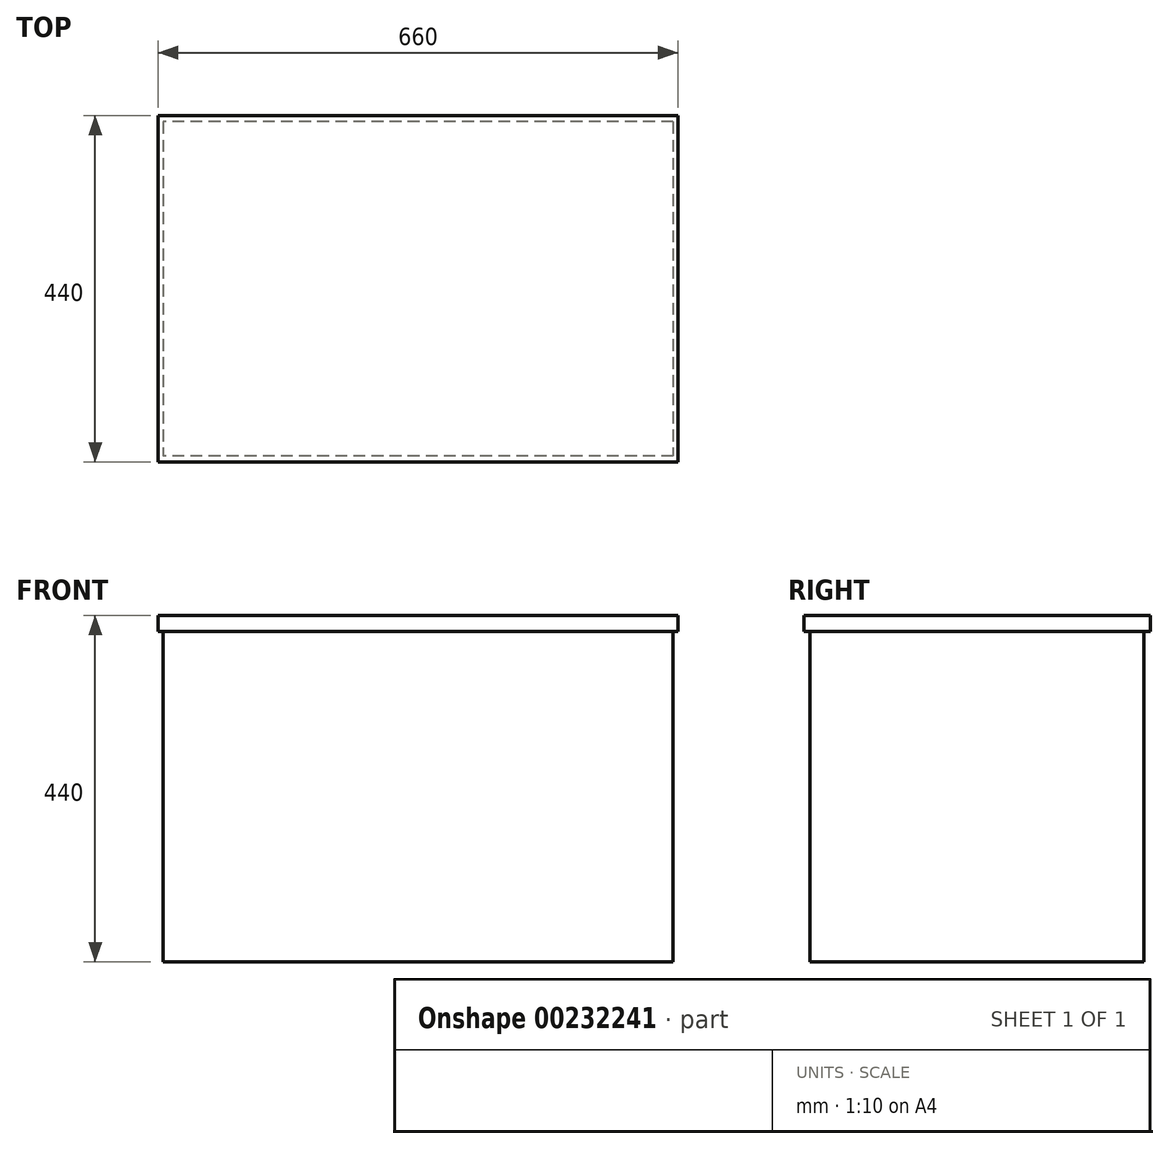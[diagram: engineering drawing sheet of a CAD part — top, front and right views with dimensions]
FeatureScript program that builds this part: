
annotation { "Feature Type Name" : "Feature", "Feature Type Description" : "" }
export const myFeature = defineFeature(function(context is Context, id is Id, definition is map)
    precondition{}
    {
        {
            var Q0;
            Q0=qCreatedBy(makeId("Top.planeOp"),FACE);
            var sketch = newSketch(context, id + "F0", { "sketchPlane" : qUnion([Q0])});
            skLineSegment(sketch, "E0.bottom", {"start": v(-323.97, -212.15) * mm, "end": v(323.97, -212.15) * mm});
            skLineSegment(sketch, "E0.top", {"start": v(-323.97, 212.15) * mm, "end": v(323.97, 212.15) * mm});
            skLineSegment(sketch, "E0.left", {"start": v(-323.97, -212.15) * mm, "end": v(-323.97, 212.15) * mm});
            skLineSegment(sketch, "E0.right", {"start": v(323.97, -212.15) * mm, "end": v(323.97, 212.15) * mm});
            skPoint(sketch, "E0.middle", {"position": v(0, 0) * mm});
            skLineSegment(sketch, "E1.bottom", {"start": v(-330, -220) * mm, "end": v(330, -220) * mm});
            skLineSegment(sketch, "E1.top", {"start": v(-330, 220) * mm, "end": v(330, 220) * mm});
            skLineSegment(sketch, "E1.left", {"start": v(-330, -220) * mm, "end": v(-330, 220) * mm});
            skLineSegment(sketch, "E1.right", {"start": v(330, -220) * mm, "end": v(330, 220) * mm});
            skSolve(sketch);
        }
        {
            var Q0;
            Q0=makeQuery(id+"F0.imprint","IMPRINT",FACE,{"disambiguationData":[TD([[makeQuery(id+"F0.imprint","IMPRINT",EDGE,{"derivedFrom":sQuery(id+"F0.wireOp",EDGE,"E0.bottom")}),1.0]])]});
            extrude(context, id + "F1", {"entities" : qUnion([Q0]), "oppositeDirection" : true, "depth" : 440 * mm});
        }
        {
            var Q0;
            Q0=makeQuery(id+"F0.imprint","IMPRINT",FACE,{"disambiguationData":[TD([[makeQuery(id+"F0.imprint","IMPRINT",EDGE,{"derivedFrom":sQuery(id+"F0.wireOp",EDGE,"E0.bottom")}),-1.0]])]});
            var Q1;
            Q1=makeQuery(id+"F0.imprint","IMPRINT",FACE,{"disambiguationData":[TD([[makeQuery(id+"F0.imprint","IMPRINT",EDGE,{"derivedFrom":sQuery(id+"F0.wireOp",EDGE,"E0.bottom")}),1.0]])]});
            extrude(context, id + "F2", {"entities" : qUnion([Q0, Q1]), "operationType" : NewBodyOperationType.ADD, "oppositeDirection" : true, "depth" : 20 * mm});
        }
    });
